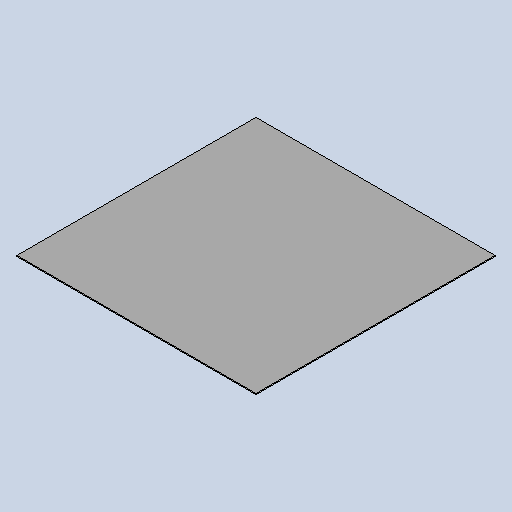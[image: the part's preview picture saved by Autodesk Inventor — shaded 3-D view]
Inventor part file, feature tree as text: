
AUTODESK INVENTOR PART (.ipt)
format: ipt  version: 2025.3 (Build 293356030, 356C)  size: 140,288 bytes
history: native  units: mm
features: other x2, sheet_metal_op x1, sketch x1
ambient origin geometry x8: Origin, YZ Plane, XZ Plane, XY Plane, X Axis, Y Axis, Z Axis, Center Point
bodies: Solid1 (feature_tree)
feature tree (4):
  sheet_metal_op  "Face1"
  sketch  "Sketch1"  dims[d2=489.0mm d3=2.0mm d18=489.0mm]
  other  "Plate1"
  other  "Definition1"
